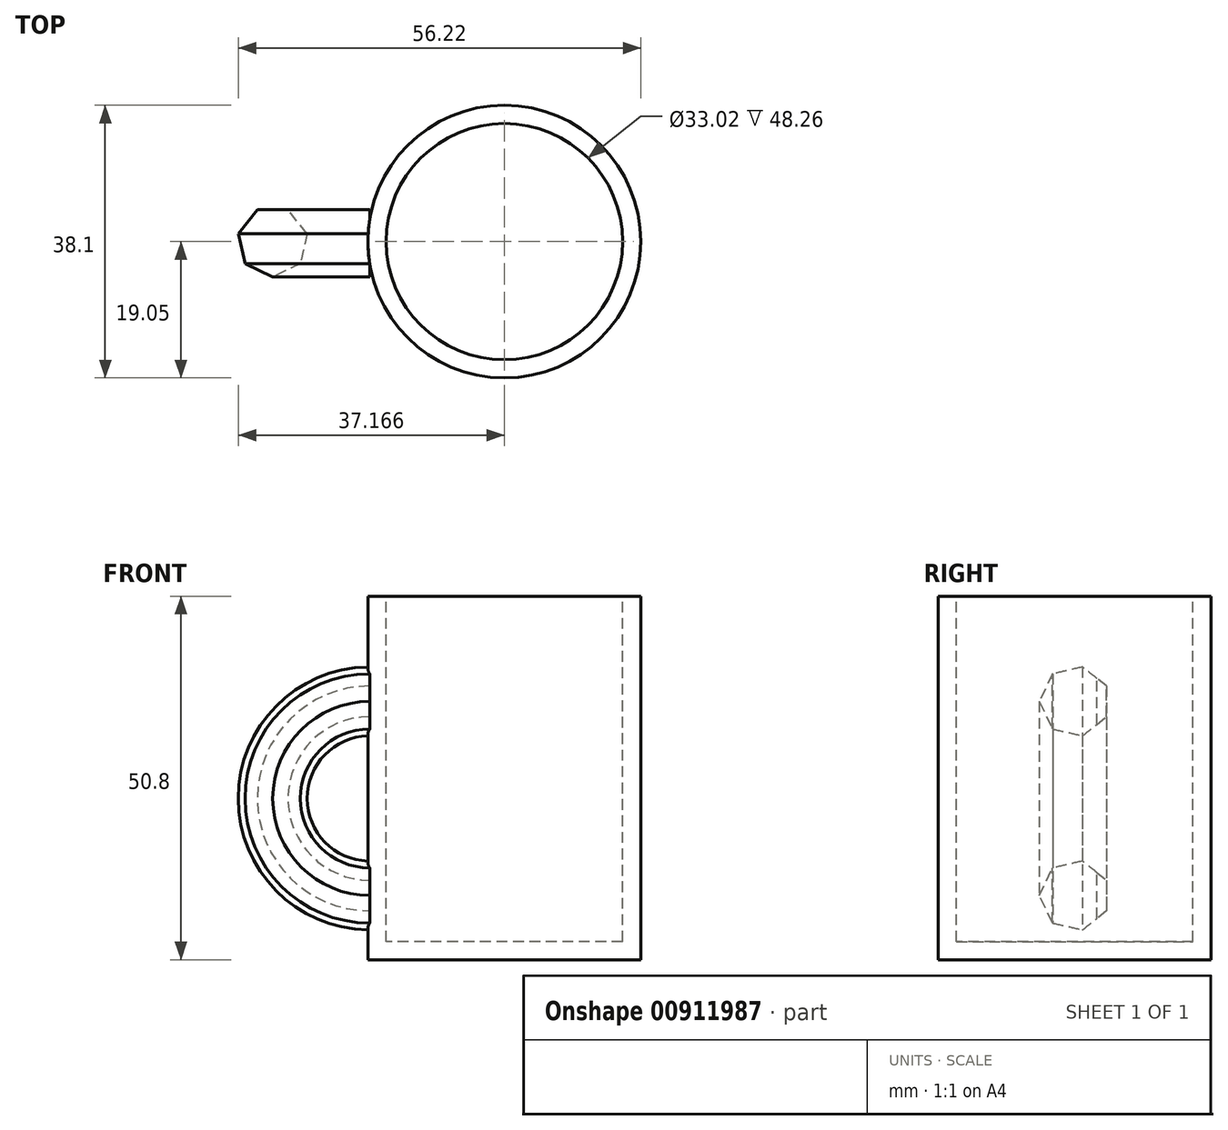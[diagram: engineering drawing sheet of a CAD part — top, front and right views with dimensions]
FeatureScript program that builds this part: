
annotation { "Feature Type Name" : "Feature", "Feature Type Description" : "" }
export const myFeature = defineFeature(function(context is Context, id is Id, definition is map)
    precondition{}
    {
        {
            var Q0;
            Q0=qCreatedBy(makeId("Front.planeOp"),FACE);
            var sketch = newSketch(context, id + "F0", { "sketchPlane" : qUnion([Q0])});
            skLineSegment(sketch, "E0.bottom", {"start": v(18.8, 55.32) * mm, "end": v(37.85, 55.32) * mm});
            skLineSegment(sketch, "E0.top", {"start": v(18.8, 4.52) * mm, "end": v(37.85, 4.52) * mm});
            skLineSegment(sketch, "E0.left", {"start": v(18.8, 55.32) * mm, "end": v(18.8, 4.52) * mm});
            skLineSegment(sketch, "E0.right", {"start": v(37.85, 55.32) * mm, "end": v(37.85, 4.52) * mm});
            skLineSegment(sketch, "E1", {"start": v(18.8, 55.32) * mm, "end": v(0, 55.32) * mm});
            skSolve(sketch);
        }
        {
            var Q0;
            Q0=qSketchRegion(id+"F0",true);
            var Q1;
            Q1=sQuery(id+"F0.wireOp",EDGE,"E0.left");
            revolve(context, id + "F1", {"surfaceOperationType" : NewSurfaceOperationType.NEW, "entities" : qUnion([Q0]), "axis" : qUnion([Q1]), "revolveType" : RevolveType.FULL});
        }
        {
            var Q0;
            Q0=makeQuery(id+"F1.opRevolve","SWEPT_FACE",FACE,{"disambiguationData":[OSD([sQuery(id+"F0.wireOp",EDGE,"E0.bottom")])]});
            shell(context, id + "F2", {"entities" : qUnion([Q0]), "thickness" : 2.54 * mm});
        }
        {
            var Q0;
            Q0=qCreatedBy(makeId("Right.planeOp"),FACE);
            var sketch = newSketch(context, id + "F3", { "sketchPlane" : qUnion([Q0])});
            skLineSegment(sketch, "E2", {"start": v(3.45, 27.05) * mm, "end": v(-4.48, 27.05) * mm, "construction": true});
            skCircle(sketch, "E3.cCircle", {"center": v(0, 13.5) * mm, "radius": 4.45 * mm, "construction": true});
            skLineSegment(sketch, "E3.0", {"start": v(-3.08, 9.64) * mm, "end": v(-4.93, 13.5) * mm});
            skLineSegment(sketch, "E3.1", {"start": v(-4.93, 13.5) * mm, "end": v(-3.07, 17.35) * mm});
            skLineSegment(sketch, "E3.2", {"start": v(-3.07, 17.35) * mm, "end": v(1.1, 18.3) * mm});
            skLineSegment(sketch, "E3.3", {"start": v(1.1, 18.3) * mm, "end": v(4.45, 15.63) * mm});
            skLineSegment(sketch, "E3.4", {"start": v(4.45, 15.63) * mm, "end": v(4.44, 11.35) * mm});
            skLineSegment(sketch, "E3.5", {"start": v(4.44, 11.35) * mm, "end": v(1.1, 8.68) * mm});
            skLineSegment(sketch, "E3.6", {"start": v(1.1, 8.68) * mm, "end": v(-3.08, 9.64) * mm});
            skPoint(sketch, "E3.0.midPoint", {"position": v(-4, 11.57) * mm});
            skSolve(sketch);
        }
        {
            var Q0;
            Q0=qSketchRegion(id+"F3",true);
            var Q1;
            Q1=sQuery(id+"F3.wireOp",EDGE,"E2");
            revolve(context, id + "F4", {"operationType" : NewBodyOperationType.ADD, "surfaceOperationType" : NewSurfaceOperationType.NEW, "entities" : qUnion([Q0]), "axis" : qUnion([Q1]), "revolveType" : RevolveType.ONE_DIRECTION, "oppositeDirection" : true, "angle" : 180 * degree});
        }
    });
